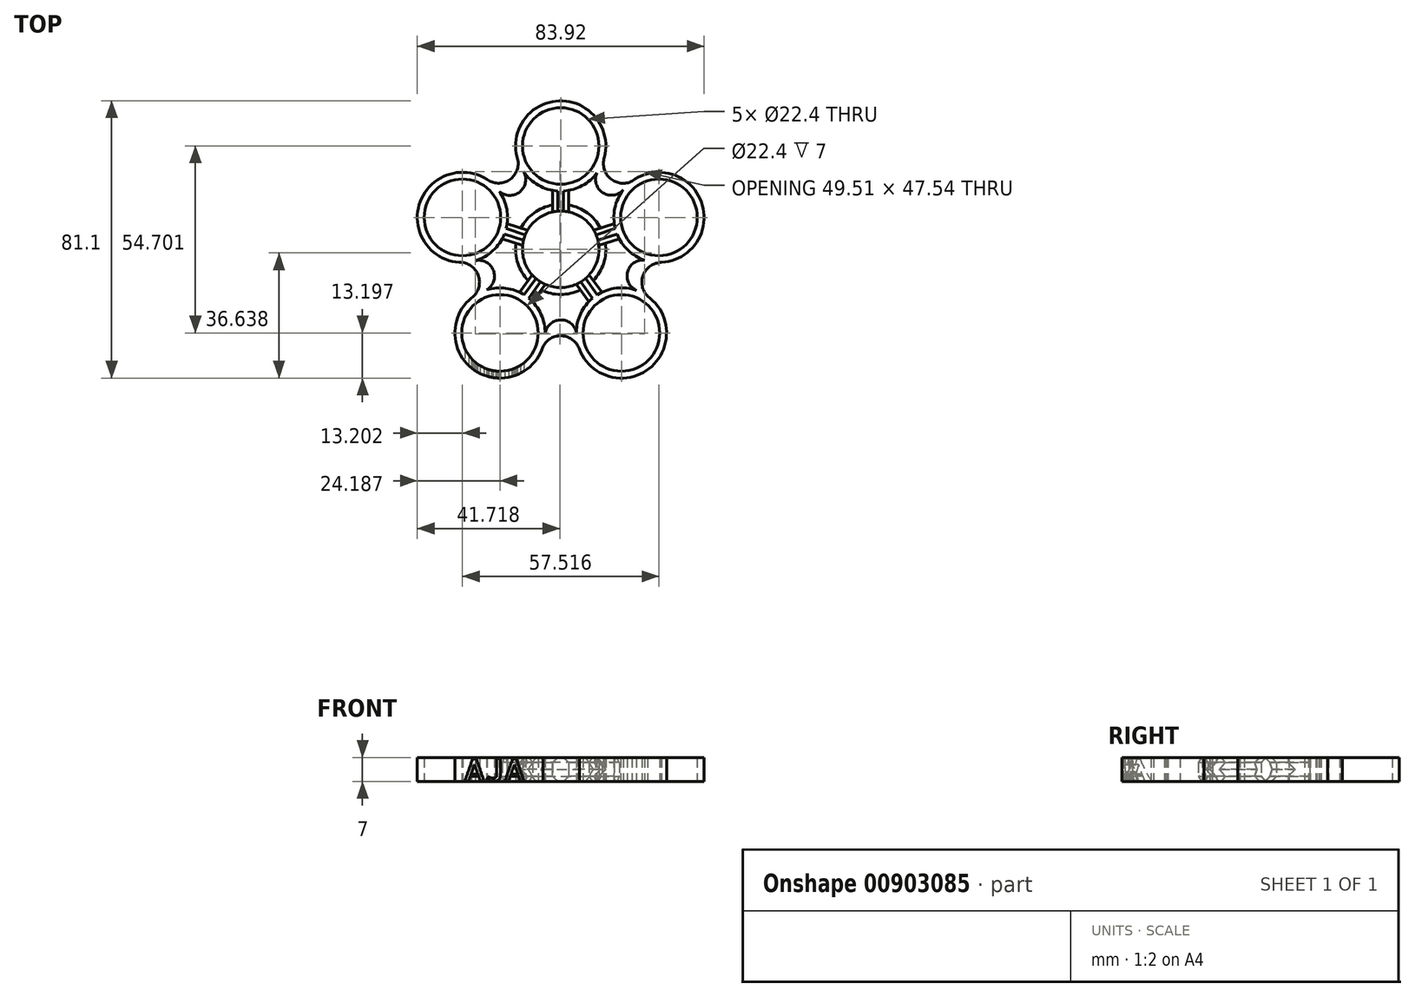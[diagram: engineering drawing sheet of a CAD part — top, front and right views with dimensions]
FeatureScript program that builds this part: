
annotation { "Feature Type Name" : "Feature", "Feature Type Description" : "" }
export const myFeature = defineFeature(function(context is Context, id is Id, definition is map)
    precondition{}
    {
        {
            var Q0;
            Q0=qCreatedBy(makeId("Top.planeOp"),FACE);
            var sketch = newSketch(context, id + "F0", { "sketchPlane" : qUnion([Q0])});
            skCircle(sketch, "E0", {"center": v(0, 0) * mm, "radius": 11.2 * mm});
            skCircle(sketch, "E1", {"center": v(0, 0) * mm, "radius": 13.2 * mm});
            skLineSegment(sketch, "E2", {"start": v(-2.34, 13) * mm, "end": v(-2.34, 18.14) * mm});
            skLineSegment(sketch, "E3", {"start": v(-2.34, 18.14) * mm, "end": v(2.33, 18.14) * mm});
            skLineSegment(sketch, "E4", {"start": v(2.33, 18.14) * mm, "end": v(2.33, 13) * mm});
            skCircle(sketch, "E5", {"center": v(0, 30.24) * mm, "radius": 13.2 * mm});
            skCircle(sketch, "E6", {"center": v(0, 30.24) * mm, "radius": 11.2 * mm});
            skCircle(sketch, "E7.1.0", {"center": v(-28.76, 9.34) * mm, "radius": 13.2 * mm});
            skCircle(sketch, "E7.1.1", {"center": v(-28.76, 9.34) * mm, "radius": 11.2 * mm});
            skLineSegment(sketch, "E7.1.2", {"start": v(-16.53, 7.82) * mm, "end": v(-11.64, 6.23) * mm});
            skLineSegment(sketch, "E7.1.3", {"start": v(-13.08, 1.78) * mm, "end": v(-17.98, 3.38) * mm});
            skLineSegment(sketch, "E7.1.4", {"start": v(-17.98, 3.38) * mm, "end": v(-16.53, 7.82) * mm});
            skCircle(sketch, "E7.2.0", {"center": v(-17.77, -24.46) * mm, "radius": 13.2 * mm});
            skCircle(sketch, "E7.2.1", {"center": v(-17.77, -24.46) * mm, "radius": 11.2 * mm});
            skLineSegment(sketch, "E7.2.2", {"start": v(-12.55, -13.3) * mm, "end": v(-9.52, -9.14) * mm});
            skLineSegment(sketch, "E7.2.3", {"start": v(-5.74, -11.89) * mm, "end": v(-8.77, -16.05) * mm});
            skLineSegment(sketch, "E7.2.4", {"start": v(-8.77, -16.05) * mm, "end": v(-12.55, -13.3) * mm});
            skCircle(sketch, "E7.3.0", {"center": v(17.77, -24.46) * mm, "radius": 13.2 * mm});
            skCircle(sketch, "E7.3.1", {"center": v(17.77, -24.46) * mm, "radius": 11.2 * mm});
            skLineSegment(sketch, "E7.3.2", {"start": v(8.78, -16.05) * mm, "end": v(5.75, -11.88) * mm});
            skLineSegment(sketch, "E7.3.3", {"start": v(9.53, -9.13) * mm, "end": v(12.56, -13.3) * mm});
            skLineSegment(sketch, "E7.3.4", {"start": v(12.56, -13.3) * mm, "end": v(8.78, -16.05) * mm});
            skCircle(sketch, "E7.4.0", {"center": v(28.76, 9.34) * mm, "radius": 13.2 * mm});
            skCircle(sketch, "E7.4.1", {"center": v(28.76, 9.34) * mm, "radius": 11.2 * mm});
            skLineSegment(sketch, "E7.4.2", {"start": v(17.97, 3.39) * mm, "end": v(13.08, 1.8) * mm});
            skLineSegment(sketch, "E7.4.3", {"start": v(11.63, 6.24) * mm, "end": v(16.53, 7.83) * mm});
            skLineSegment(sketch, "E7.4.4", {"start": v(16.53, 7.83) * mm, "end": v(17.97, 3.39) * mm});
            skArc(sketch, "E8", {"start": v(-17.98, 16.96) * mm, "mid": v(-11.96, 16.83) * mm, "end": v(-10.87, 22.75) * mm});
            skArc(sketch, "E9", {"start": v(-21.6, 20.43) * mm, "mid": v(-15.2, 20.23) * mm, "end": v(-12.5, 26.02) * mm});
            skArc(sketch, "E10.1.0", {"start": v(-26.1, -14.22) * mm, "mid": v(-23.93, -8.2) * mm, "end": v(-28.62, -3.86) * mm});
            skArc(sketch, "E10.1.1", {"start": v(-21.68, -11.86) * mm, "mid": v(-19.7, -6.17) * mm, "end": v(-25, -3.3) * mm});
            skArc(sketch, "E10.2.0", {"start": v(5.46, -29.22) * mm, "mid": v(0.41, -25.3) * mm, "end": v(-5.18, -28.4) * mm});
            skArc(sketch, "E10.2.1", {"start": v(4.57, -24.29) * mm, "mid": v(-0.22, -20.65) * mm, "end": v(-4.58, -24.8) * mm});
            skArc(sketch, "E10.3.0", {"start": v(29.48, -3.84) * mm, "mid": v(24.19, -7.43) * mm, "end": v(25.42, -13.7) * mm});
            skArc(sketch, "E10.3.1", {"start": v(24.51, -3.15) * mm, "mid": v(19.57, -6.59) * mm, "end": v(22.17, -12.02) * mm});
            skArc(sketch, "E10.4.0", {"start": v(12.76, 26.85) * mm, "mid": v(14.54, 20.7) * mm, "end": v(20.88, 19.94) * mm});
            skArc(sketch, "E10.4.1", {"start": v(10.57, 22.34) * mm, "mid": v(12.31, 16.58) * mm, "end": v(18.28, 17.37) * mm});
            skSolve(sketch);
        }
        {
            var Q0;
            {var subQ0=sQuery(id+"F0.wireOp",EDGE,"E8");Q0=makeQuery(id+"F0.imprint","IMPRINT",FACE,{"disambiguationData":[TD([[makeQuery(id+"F0.imprint","IMPRINT",EDGE,{"derivedFrom":subQ0}),1.0]])]});}
            var Q1;
            Q1=makeQuery(id+"F0.imprint","IMPRINT",FACE,{"disambiguationData":[TD([[makeQuery(id+"F0.imprint","IMPRINT",EDGE,{"derivedFrom":sQuery(id+"F0.wireOp",EDGE,"E7.1.1")}),-1.0]])]});
            var Q2;
            {var subQ5=sQuery(id+"F0.wireOp",EDGE,"E7.1.4");Q2=makeQuery(id+"F0.imprint","IMPRINT",FACE,{"disambiguationData":[TD([[makeQuery(id+"F0.imprint","IMPRINT",EDGE,{"derivedFrom":subQ5}),-1.0]])]});}
            var Q3;
            {var subQ0=sQuery(id+"F0.wireOp",EDGE,"E7.1.2");var subQ1=sQuery(id+"F0.wireOp",EDGE,"E1");var subQ2=makeQuery(id+"F0.imprint","INTERSECT",VERTEX,{"derivedFrom":[subQ1,subQ0]});Q3=makeQuery(id+"F0.imprint","IMPRINT",FACE,{"disambiguationData":[TD([[makeQuery(id+"F0.imprint","IMPRINT",EDGE,{"disambiguationData":[TD([[subQ2,-1.0]])],"derivedFrom":subQ1}),-1.0]])]});}
            var Q4;
            {var subQ0=sQuery(id+"F0.wireOp",EDGE,"E3");Q4=makeQuery(id+"F0.imprint","IMPRINT",FACE,{"disambiguationData":[TD([[makeQuery(id+"F0.imprint","IMPRINT",EDGE,{"derivedFrom":subQ0}),-1.0]])]});}
            var Q5;
            {var subQ4=sQuery(id+"F0.wireOp",EDGE,"E3");Q5=makeQuery(id+"F0.imprint","IMPRINT",FACE,{"disambiguationData":[TD([[makeQuery(id+"F0.imprint","IMPRINT",EDGE,{"derivedFrom":subQ4}),1.0]])]});}
            var Q6;
            {var subQ0=sQuery(id+"F0.wireOp",EDGE,"E10.4.1");Q6=makeQuery(id+"F0.imprint","IMPRINT",FACE,{"disambiguationData":[TD([[makeQuery(id+"F0.imprint","IMPRINT",EDGE,{"derivedFrom":subQ0}),1.0]])]});}
            var Q7;
            {var subQ5=sQuery(id+"F0.wireOp",EDGE,"E7.4.4");Q7=makeQuery(id+"F0.imprint","IMPRINT",FACE,{"disambiguationData":[TD([[makeQuery(id+"F0.imprint","IMPRINT",EDGE,{"derivedFrom":subQ5}),-1.0]])]});}
            var Q8;
            {var subQ5=sQuery(id+"F0.wireOp",EDGE,"E7.3.4");Q8=makeQuery(id+"F0.imprint","IMPRINT",FACE,{"disambiguationData":[TD([[makeQuery(id+"F0.imprint","IMPRINT",EDGE,{"derivedFrom":subQ5}),-1.0]])]});}
            var Q9;
            {var subQ5=sQuery(id+"F0.wireOp",EDGE,"E7.2.4");Q9=makeQuery(id+"F0.imprint","IMPRINT",FACE,{"disambiguationData":[TD([[makeQuery(id+"F0.imprint","IMPRINT",EDGE,{"derivedFrom":subQ5}),-1.0]])]});}
            var Q10;
            {var subQ0=sQuery(id+"F0.wireOp",EDGE,"E7.2.2");var subQ1=sQuery(id+"F0.wireOp",EDGE,"E1");var subQ2=makeQuery(id+"F0.imprint","INTERSECT",VERTEX,{"derivedFrom":[subQ1,subQ0]});Q10=makeQuery(id+"F0.imprint","IMPRINT",FACE,{"disambiguationData":[TD([[makeQuery(id+"F0.imprint","IMPRINT",EDGE,{"disambiguationData":[TD([[subQ2,-1.0]])],"derivedFrom":subQ1}),-1.0]])]});}
            var Q11;
            Q11=makeQuery(id+"F0.imprint","IMPRINT",FACE,{"disambiguationData":[TD([[makeQuery(id+"F0.imprint","IMPRINT",EDGE,{"derivedFrom":sQuery(id+"F0.wireOp",EDGE,"E0")}),-1.0]])]});
            var Q12;
            {var subQ0=sQuery(id+"F0.wireOp",EDGE,"E7.4.2");var subQ1=sQuery(id+"F0.wireOp",EDGE,"E1");var subQ2=makeQuery(id+"F0.imprint","INTERSECT",VERTEX,{"derivedFrom":[subQ1,subQ0]});Q12=makeQuery(id+"F0.imprint","IMPRINT",FACE,{"disambiguationData":[TD([[makeQuery(id+"F0.imprint","IMPRINT",EDGE,{"disambiguationData":[TD([[subQ2,-1.0]])],"derivedFrom":subQ1}),-1.0]])]});}
            var Q13;
            {var subQ0=sQuery(id+"F0.wireOp",EDGE,"E2");var subQ1=sQuery(id+"F0.wireOp",EDGE,"E1");var subQ2=makeQuery(id+"F0.imprint","INTERSECT",VERTEX,{"derivedFrom":[subQ1,subQ0]});Q13=makeQuery(id+"F0.imprint","IMPRINT",FACE,{"disambiguationData":[TD([[makeQuery(id+"F0.imprint","IMPRINT",EDGE,{"disambiguationData":[TD([[subQ2,1.0]])],"derivedFrom":subQ1}),-1.0]])]});}
            var Q14;
            {var subQ0=sQuery(id+"F0.wireOp",EDGE,"E7.3.2");var subQ1=sQuery(id+"F0.wireOp",EDGE,"E1");var subQ2=makeQuery(id+"F0.imprint","INTERSECT",VERTEX,{"derivedFrom":[subQ1,subQ0]});Q14=makeQuery(id+"F0.imprint","IMPRINT",FACE,{"disambiguationData":[TD([[makeQuery(id+"F0.imprint","IMPRINT",EDGE,{"disambiguationData":[TD([[subQ2,-1.0]])],"derivedFrom":subQ1}),-1.0]])]});}
            var Q15;
            Q15=makeQuery(id+"F0.imprint","IMPRINT",FACE,{"disambiguationData":[TD([[makeQuery(id+"F0.imprint","IMPRINT",EDGE,{"derivedFrom":sQuery(id+"F0.wireOp",EDGE,"E7.3.1")}),-1.0]])]});
            var Q16;
            {var subQ3=sQuery(id+"F0.wireOp",EDGE,"E10.2.1");Q16=makeQuery(id+"F0.imprint","IMPRINT",FACE,{"disambiguationData":[TD([[makeQuery(id+"F0.imprint","IMPRINT",EDGE,{"derivedFrom":subQ3}),1.0]])]});}
            var Q17;
            Q17=makeQuery(id+"F0.imprint","IMPRINT",FACE,{"disambiguationData":[TD([[makeQuery(id+"F0.imprint","IMPRINT",EDGE,{"derivedFrom":sQuery(id+"F0.wireOp",EDGE,"E7.2.1")}),-1.0]])]});
            var Q18;
            {var subQ3=sQuery(id+"F0.wireOp",EDGE,"E10.1.1");Q18=makeQuery(id+"F0.imprint","IMPRINT",FACE,{"disambiguationData":[TD([[makeQuery(id+"F0.imprint","IMPRINT",EDGE,{"derivedFrom":subQ3}),1.0]])]});}
            var Q19;
            Q19=makeQuery(id+"F0.imprint","IMPRINT",FACE,{"disambiguationData":[TD([[makeQuery(id+"F0.imprint","IMPRINT",EDGE,{"derivedFrom":sQuery(id+"F0.wireOp",EDGE,"E7.4.1")}),-1.0]])]});
            var Q20;
            {var subQ3=sQuery(id+"F0.wireOp",EDGE,"E10.3.1");Q20=makeQuery(id+"F0.imprint","IMPRINT",FACE,{"disambiguationData":[TD([[makeQuery(id+"F0.imprint","IMPRINT",EDGE,{"derivedFrom":subQ3}),1.0]])]});}
            extrude(context, id + "F1", {"entities" : qUnion([Q0, Q1, Q2, Q3, Q4, Q5, Q6, Q7, Q8, Q9, Q10, Q11, Q12, Q13, Q14, Q15, Q16, Q17, Q18, Q19, Q20]), "depth" : 7 * mm, "offsetDistance" : 25 * mm});
        }
        {
            var Q0;
            {var subQ0=sQuery(id+"F0.wireOp",EDGE,"E1");Q0=makeQuery(id+"F1.opExtrude","CAP_EDGE",EDGE,{"disambiguationData":[OSD([subQ0]),TDD([makeQuery(id+"F0.imprint","IMPRINT",EDGE,{"disambiguationData":[TD([[makeQuery(id+"F0.imprint","INTERSECT",VERTEX,{"derivedFrom":[subQ0,sQuery(id+"F0.wireOp",EDGE,"E7.3.3")]}),-1.0]])],"derivedFrom":subQ0})])],"isStart":false});}
            var Q1;
            {var subQ0=sQuery(id+"F0.wireOp",EDGE,"E1");Q1=makeQuery(id+"F1.opExtrude","CAP_EDGE",EDGE,{"disambiguationData":[OSD([subQ0]),TDD([makeQuery(id+"F0.imprint","IMPRINT",EDGE,{"disambiguationData":[TD([[makeQuery(id+"F0.imprint","INTERSECT",VERTEX,{"derivedFrom":[subQ0,sQuery(id+"F0.wireOp",EDGE,"E4")]}),1.0]])],"derivedFrom":subQ0})])],"isStart":false});}
            var Q2;
            {var subQ0=sQuery(id+"F0.wireOp",EDGE,"E1");Q2=makeQuery(id+"F1.opExtrude","CAP_EDGE",EDGE,{"disambiguationData":[OSD([subQ0]),TDD([makeQuery(id+"F0.imprint","IMPRINT",EDGE,{"disambiguationData":[TD([[makeQuery(id+"F0.imprint","INTERSECT",VERTEX,{"derivedFrom":[subQ0,sQuery(id+"F0.wireOp",EDGE,"E2")]}),-1.0]])],"derivedFrom":subQ0})])],"isStart":false});}
            var Q3;
            {var subQ0=sQuery(id+"F0.wireOp",EDGE,"E1");Q3=makeQuery(id+"F1.opExtrude","CAP_EDGE",EDGE,{"disambiguationData":[OSD([subQ0]),TDD([makeQuery(id+"F0.imprint","IMPRINT",EDGE,{"disambiguationData":[TD([[makeQuery(id+"F0.imprint","INTERSECT",VERTEX,{"derivedFrom":[subQ0,sQuery(id+"F0.wireOp",EDGE,"E7.1.3")]}),-1.0]])],"derivedFrom":subQ0})])],"isStart":false});}
            var Q4;
            {var subQ0=sQuery(id+"F0.wireOp",EDGE,"E1");Q4=makeQuery(id+"F1.opExtrude","CAP_EDGE",EDGE,{"disambiguationData":[OSD([subQ0]),TDD([makeQuery(id+"F0.imprint","IMPRINT",EDGE,{"disambiguationData":[TD([[makeQuery(id+"F0.imprint","INTERSECT",VERTEX,{"derivedFrom":[subQ0,sQuery(id+"F0.wireOp",EDGE,"E7.2.3")]}),-1.0]])],"derivedFrom":subQ0})])],"isStart":false});}
            chamfer(context, id + "F2", {"entities" : qUnion([Q0, Q1, Q2, Q3, Q4]), "width" : 3.5 * mm, "tangentPropagation" : true});
        }
        {
            var Q0;
            {var subQ0=sQuery(id+"F0.wireOp",EDGE,"E1");Q0=makeQuery(id+"F1.opExtrude","CAP_EDGE",EDGE,{"disambiguationData":[OSD([subQ0]),TDD([makeQuery(id+"F0.imprint","IMPRINT",EDGE,{"disambiguationData":[TD([[makeQuery(id+"F0.imprint","INTERSECT",VERTEX,{"derivedFrom":[subQ0,sQuery(id+"F0.wireOp",EDGE,"E4")]}),1.0]])],"derivedFrom":subQ0})])],"isStart":true});}
            var Q1;
            {var subQ0=sQuery(id+"F0.wireOp",EDGE,"E1");Q1=makeQuery(id+"F1.opExtrude","CAP_EDGE",EDGE,{"disambiguationData":[OSD([subQ0]),TDD([makeQuery(id+"F0.imprint","IMPRINT",EDGE,{"disambiguationData":[TD([[makeQuery(id+"F0.imprint","INTERSECT",VERTEX,{"derivedFrom":[subQ0,sQuery(id+"F0.wireOp",EDGE,"E2")]}),-1.0]])],"derivedFrom":subQ0})])],"isStart":true});}
            var Q2;
            {var subQ0=sQuery(id+"F0.wireOp",EDGE,"E1");Q2=makeQuery(id+"F1.opExtrude","CAP_EDGE",EDGE,{"disambiguationData":[OSD([subQ0]),TDD([makeQuery(id+"F0.imprint","IMPRINT",EDGE,{"disambiguationData":[TD([[makeQuery(id+"F0.imprint","INTERSECT",VERTEX,{"derivedFrom":[subQ0,sQuery(id+"F0.wireOp",EDGE,"E7.1.3")]}),-1.0]])],"derivedFrom":subQ0})])],"isStart":true});}
            var Q3;
            {var subQ0=sQuery(id+"F0.wireOp",EDGE,"E1");Q3=makeQuery(id+"F1.opExtrude","CAP_EDGE",EDGE,{"disambiguationData":[OSD([subQ0]),TDD([makeQuery(id+"F0.imprint","IMPRINT",EDGE,{"disambiguationData":[TD([[makeQuery(id+"F0.imprint","INTERSECT",VERTEX,{"derivedFrom":[subQ0,sQuery(id+"F0.wireOp",EDGE,"E7.2.3")]}),-1.0]])],"derivedFrom":subQ0})])],"isStart":true});}
            var Q4;
            {var subQ0=sQuery(id+"F0.wireOp",EDGE,"E1");Q4=makeQuery(id+"F1.opExtrude","CAP_EDGE",EDGE,{"disambiguationData":[OSD([subQ0]),TDD([makeQuery(id+"F0.imprint","IMPRINT",EDGE,{"disambiguationData":[TD([[makeQuery(id+"F0.imprint","INTERSECT",VERTEX,{"derivedFrom":[subQ0,sQuery(id+"F0.wireOp",EDGE,"E7.3.3")]}),-1.0]])],"derivedFrom":subQ0})])],"isStart":true});}
            chamfer(context, id + "F3", {"entities" : qUnion([Q0, Q1, Q2, Q3, Q4]), "width" : 3.5 * mm, "tangentPropagation" : true});
        }
        {
            var Q0;
            Q0=makeQuery(id+"F1.opExtrude","CAP_EDGE",EDGE,{"disambiguationData":[OSD([sQuery(id+"F0.wireOp",EDGE,"E10.3.0")])],"isStart":true});
            var Q1;
            Q1=makeQuery(id+"F1.opExtrude","CAP_EDGE",EDGE,{"disambiguationData":[OSD([sQuery(id+"F0.wireOp",EDGE,"E10.4.0")])],"isStart":true});
            var Q2;
            Q2=makeQuery(id+"F1.opExtrude","CAP_EDGE",EDGE,{"disambiguationData":[OSD([sQuery(id+"F0.wireOp",EDGE,"E9")])],"isStart":true});
            var Q3;
            Q3=makeQuery(id+"F1.opExtrude","CAP_EDGE",EDGE,{"disambiguationData":[OSD([sQuery(id+"F0.wireOp",EDGE,"E10.1.0")])],"isStart":true});
            var Q4;
            Q4=makeQuery(id+"F1.opExtrude","CAP_EDGE",EDGE,{"disambiguationData":[OSD([sQuery(id+"F0.wireOp",EDGE,"E10.2.0")])],"isStart":true});
            fillet(context, id + "F4", {"entities" : qUnion([Q0, Q1, Q2, Q3, Q4]), "radius" : 0.02 * mm, "tangentPropagation" : true, "allowEdgeOverflow" : false});
        }
        {
            var Q0;
            Q0=makeQuery(id+"F1.opExtrude","CAP_EDGE",EDGE,{"disambiguationData":[OSD([sQuery(id+"F0.wireOp",EDGE,"E4")])],"isStart":true});
            var Q1;
            Q1=makeQuery(id+"F1.opExtrude","CAP_EDGE",EDGE,{"disambiguationData":[OSD([sQuery(id+"F0.wireOp",EDGE,"E2")])],"isStart":true});
            var Q2;
            Q2=makeQuery(id+"F1.opExtrude","CAP_EDGE",EDGE,{"disambiguationData":[OSD([sQuery(id+"F0.wireOp",EDGE,"E7.1.2")])],"isStart":true});
            var Q3;
            Q3=makeQuery(id+"F1.opExtrude","CAP_EDGE",EDGE,{"disambiguationData":[OSD([sQuery(id+"F0.wireOp",EDGE,"E7.1.3")])],"isStart":true});
            var Q4;
            Q4=makeQuery(id+"F1.opExtrude","CAP_EDGE",EDGE,{"disambiguationData":[OSD([sQuery(id+"F0.wireOp",EDGE,"E7.2.2")])],"isStart":true});
            var Q5;
            Q5=makeQuery(id+"F1.opExtrude","CAP_EDGE",EDGE,{"disambiguationData":[OSD([sQuery(id+"F0.wireOp",EDGE,"E7.2.3")])],"isStart":true});
            var Q6;
            Q6=makeQuery(id+"F1.opExtrude","CAP_EDGE",EDGE,{"disambiguationData":[OSD([sQuery(id+"F0.wireOp",EDGE,"E7.3.2")])],"isStart":true});
            var Q7;
            Q7=makeQuery(id+"F1.opExtrude","CAP_EDGE",EDGE,{"disambiguationData":[OSD([sQuery(id+"F0.wireOp",EDGE,"E7.3.3")])],"isStart":true});
            var Q8;
            Q8=makeQuery(id+"F1.opExtrude","CAP_EDGE",EDGE,{"disambiguationData":[OSD([sQuery(id+"F0.wireOp",EDGE,"E7.4.2")])],"isStart":true});
            var Q9;
            Q9=makeQuery(id+"F1.opExtrude","CAP_EDGE",EDGE,{"disambiguationData":[OSD([sQuery(id+"F0.wireOp",EDGE,"E7.4.3")])],"isStart":true});
            chamfer(context, id + "F5", {"entities" : qUnion([Q0, Q1, Q2, Q3, Q4, Q5, Q6, Q7, Q8, Q9]), "width" : 1.5 * mm, "tangentPropagation" : true});
        }
        {
            var Q0;
            Q0=makeQuery(id+"F1.opExtrude","CAP_EDGE",EDGE,{"disambiguationData":[OSD([sQuery(id+"F0.wireOp",EDGE,"E7.1.2")])],"isStart":false});
            var Q1;
            Q1=makeQuery(id+"F1.opExtrude","CAP_EDGE",EDGE,{"disambiguationData":[OSD([sQuery(id+"F0.wireOp",EDGE,"E7.1.3")])],"isStart":false});
            var Q2;
            Q2=makeQuery(id+"F1.opExtrude","CAP_EDGE",EDGE,{"disambiguationData":[OSD([sQuery(id+"F0.wireOp",EDGE,"E2")])],"isStart":false});
            var Q3;
            Q3=makeQuery(id+"F1.opExtrude","CAP_EDGE",EDGE,{"disambiguationData":[OSD([sQuery(id+"F0.wireOp",EDGE,"E4")])],"isStart":false});
            var Q4;
            Q4=makeQuery(id+"F1.opExtrude","CAP_EDGE",EDGE,{"disambiguationData":[OSD([sQuery(id+"F0.wireOp",EDGE,"E7.4.3")])],"isStart":false});
            var Q5;
            Q5=makeQuery(id+"F1.opExtrude","CAP_EDGE",EDGE,{"disambiguationData":[OSD([sQuery(id+"F0.wireOp",EDGE,"E7.4.2")])],"isStart":false});
            var Q6;
            Q6=makeQuery(id+"F1.opExtrude","CAP_EDGE",EDGE,{"disambiguationData":[OSD([sQuery(id+"F0.wireOp",EDGE,"E7.3.3")])],"isStart":false});
            var Q7;
            Q7=makeQuery(id+"F1.opExtrude","CAP_EDGE",EDGE,{"disambiguationData":[OSD([sQuery(id+"F0.wireOp",EDGE,"E7.3.2")])],"isStart":false});
            var Q8;
            Q8=makeQuery(id+"F1.opExtrude","CAP_EDGE",EDGE,{"disambiguationData":[OSD([sQuery(id+"F0.wireOp",EDGE,"E7.2.3")])],"isStart":false});
            var Q9;
            Q9=makeQuery(id+"F1.opExtrude","CAP_EDGE",EDGE,{"disambiguationData":[OSD([sQuery(id+"F0.wireOp",EDGE,"E7.2.2")])],"isStart":false});
            chamfer(context, id + "F6", {"entities" : qUnion([Q0, Q1, Q2, Q3, Q4, Q5, Q6, Q7, Q8, Q9]), "width" : 1.5 * mm, "tangentPropagation" : true});
        }
        {
            var Q0;
            Q0=qCreatedBy(makeId("Front.planeOp"),FACE);
            cPlane(context, id + "F7", {"entities" : qUnion([Q0]), "cplaneType" : CPlaneType.OFFSET, "offset" : 49.6 * mm, "width" : 150 * mm, "height" : 150 * mm});
        }
        {
            var Q0;
            Q0=qCreatedBy(id+"F7.planeOp",FACE);
            var sketch = newSketch(context, id + "F8", { "sketchPlane" : qUnion([Q0])});
            skText(sketch, "E11", { "text": "AJA\n", "fontName": "AllertaStencil-Regular.ttf"});
            const initialGuessF8  = {"E11": [-0.0286, 0.0001, 1, 0, 0.00652]};
            skSetInitialGuess(sketch, initialGuessF8);
            skSolve(sketch);
        }
        {
            var Q0;
            Q0=qSketchRegion(id+"F8",true);
            extrude(context, id + "F9", {"entities" : qUnion([Q0]), "operationType" : NewBodyOperationType.REMOVE, "oppositeDirection" : true, "depth" : 25 * mm, "offsetDistance" : 25 * mm});
        }
    });
